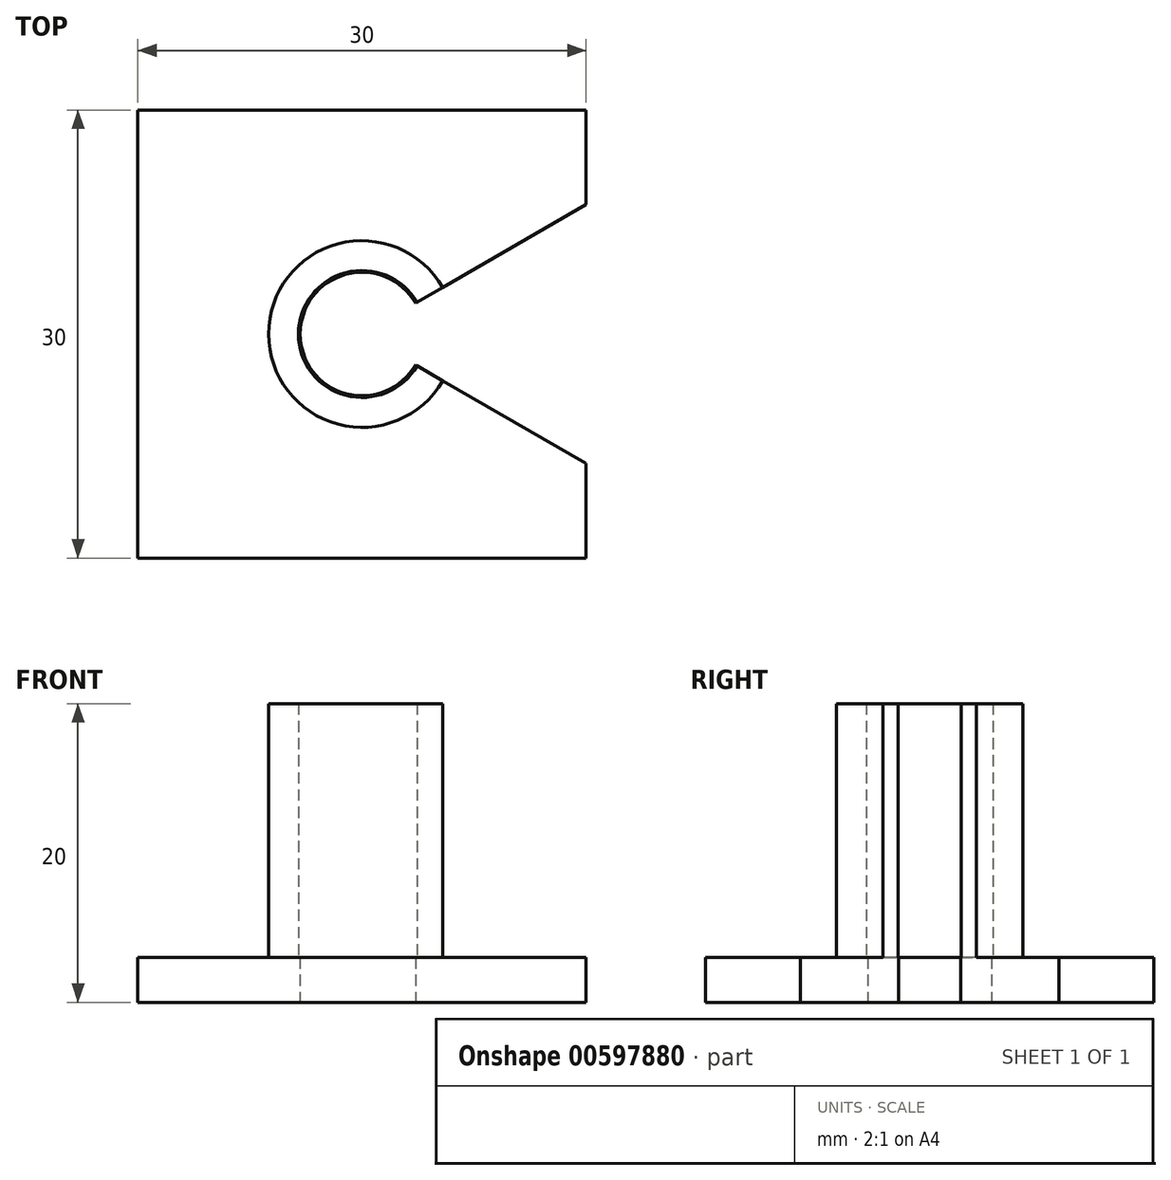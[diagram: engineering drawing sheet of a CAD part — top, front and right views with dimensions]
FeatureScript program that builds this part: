
annotation { "Feature Type Name" : "Feature", "Feature Type Description" : "" }
export const myFeature = defineFeature(function(context is Context, id is Id, definition is map)
    precondition{}
    {
        {
            var Q0;
            Q0=qCreatedBy(makeId("Top.planeOp"),FACE);
            var sketch = newSketch(context, id + "F0", { "sketchPlane" : qUnion([Q0])});
            skCircle(sketch, "E0", {"center": v(0, 0) * mm, "radius": 4.25 * mm});
            skCircle(sketch, "E1", {"center": v(0, 0) * mm, "radius": 6.25 * mm});
            skSolve(sketch);
        }
        {
            var Q0;
            Q0 = qSketchRegion(id + "F0", true);
            extrude(context, id + "F1", {"entities" : qUnion([Q0]), "depth" : 20 * mm, "offsetDistance" : 25 * mm});
        }
        {
            var Q0;
            Q0=qCreatedBy(makeId("Top.planeOp"),FACE);
            var sketch = newSketch(context, id + "F2", { "sketchPlane" : qUnion([Q0])});
            skLineSegment(sketch, "E2.bottom", {"start": v(15, -15) * mm, "end": v(-15, -15) * mm});
            skLineSegment(sketch, "E2.top", {"start": v(15, 15) * mm, "end": v(-15, 15) * mm});
            skLineSegment(sketch, "E2.left", {"start": v(15, -15) * mm, "end": v(15, 15) * mm});
            skLineSegment(sketch, "E2.right", {"start": v(-15, -15) * mm, "end": v(-15, 15) * mm});
            skPoint(sketch, "E2.middle", {"position": v(0, 0) * mm});
            skSolve(sketch);
        }
        {
            var Q0;
            Q0 = qSketchRegion(id + "F2", true);
            extrude(context, id + "F3", {"entities" : qUnion([Q0]), "operationType" : NewBodyOperationType.ADD, "depth" : 3 * mm, "offsetDistance" : 25 * mm});
        }
        {
            var Q0;
            Q0=qCreatedBy(makeId("Top.planeOp"),FACE);
            var sketch = newSketch(context, id + "F4", { "sketchPlane" : qUnion([Q0])});
            skCircle(sketch, "E3", {"center": v(0, 0) * mm, "radius": 4.13 * mm});
            skSolve(sketch);
        }
        {
            var Q0;
            Q0 = qSketchRegion(id + "F4", true);
            extrude(context, id + "F5", {"entities" : qUnion([Q0]), "operationType" : NewBodyOperationType.REMOVE, "endBound" : BoundingType.THROUGH_ALL, "depth" : 25 * mm, "offsetDistance" : 25 * mm});
        }
        {
            var Q0;
            Q0=qCreatedBy(makeId("Top.planeOp"),FACE);
            var sketch = newSketch(context, id + "F6", { "sketchPlane" : qUnion([Q0])});
            skCircle(sketch, "E4.cCircle", {"center": v(42.44, 0) * mm, "radius": 21.22 * mm, "construction": true});
            skLineSegment(sketch, "E4.0", {"start": v(63.67, 36.76) * mm, "end": v(63.67, -36.76) * mm});
            skLineSegment(sketch, "E4.1", {"start": v(63.67, -36.76) * mm, "end": v(0, 0) * mm});
            skLineSegment(sketch, "E4.2", {"start": v(0, 0) * mm, "end": v(63.67, 36.76) * mm});
            skPoint(sketch, "E4.0.midPoint", {"position": v(63.67, 0) * mm});
            skSolve(sketch);
        }
        {
            var Q0;
            Q0 = qSketchRegion(id + "F6", true);
            extrude(context, id + "F7", {"entities" : qUnion([Q0]), "operationType" : NewBodyOperationType.REMOVE, "depth" : 25 * mm, "offsetDistance" : 25 * mm});
        }
    });
